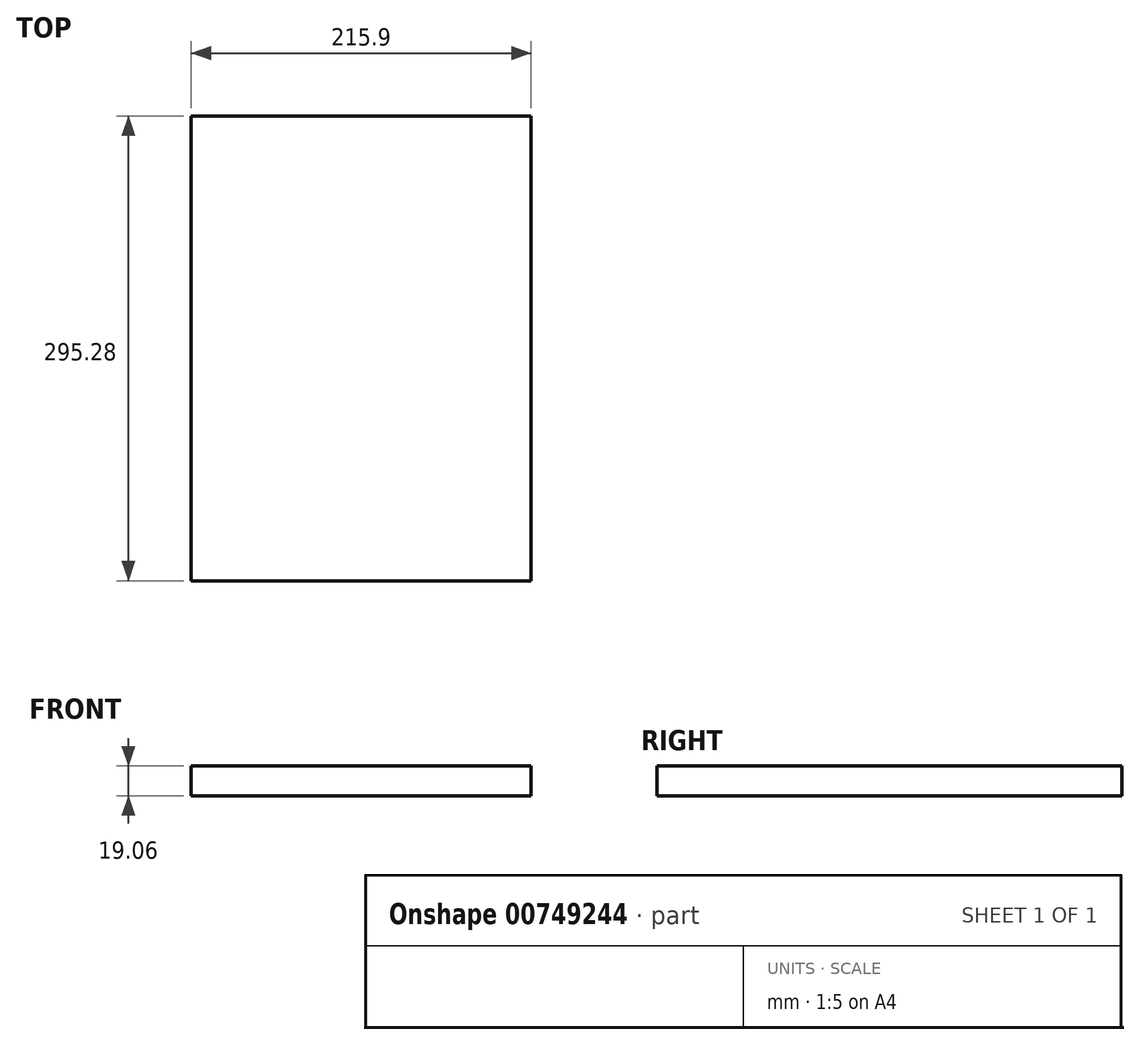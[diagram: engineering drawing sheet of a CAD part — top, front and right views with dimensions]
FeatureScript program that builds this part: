
annotation { "Feature Type Name" : "Feature", "Feature Type Description" : "" }
export const myFeature = defineFeature(function(context is Context, id is Id, definition is map)
    precondition{}
    {
        {
            var Q0;
            Q0=qCreatedBy(makeId("Front.planeOp"),FACE);
            var sketch = newSketch(context, id + "F0", { "sketchPlane" : qUnion([Q0])});
            skLineSegment(sketch, "E0.bottom", {"start": v(107.95, 9.53) * mm, "end": v(-107.95, 9.53) * mm});
            skLineSegment(sketch, "E0.top", {"start": v(107.95, -9.53) * mm, "end": v(-107.95, -9.53) * mm});
            skLineSegment(sketch, "E0.left", {"start": v(107.95, 9.53) * mm, "end": v(107.95, -9.53) * mm});
            skLineSegment(sketch, "E0.right", {"start": v(-107.95, 9.53) * mm, "end": v(-107.95, -9.53) * mm});
            skPoint(sketch, "E0.middle", {"position": v(0, 0) * mm});
            skSolve(sketch);
        }
        {
            var Q0;
            Q0 = qSketchRegion(id + "F0", true);
            extrude(context, id + "F1", {"entities" : qUnion([Q0]), "depth" : 295.27 * mm, "offsetDistance" : 25.4 * mm});
        }
    });
